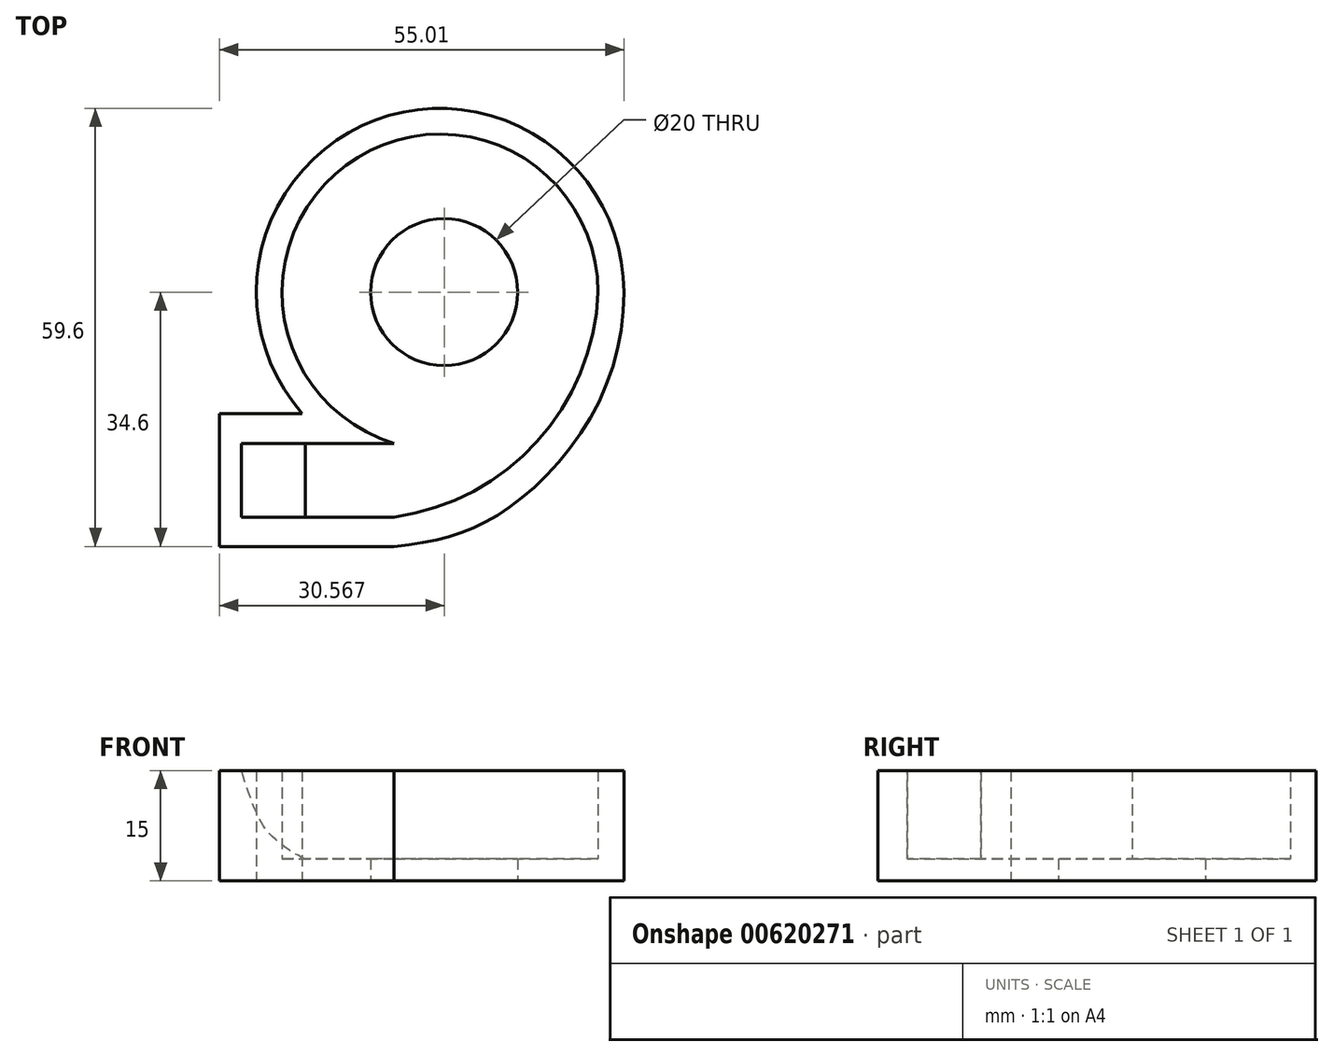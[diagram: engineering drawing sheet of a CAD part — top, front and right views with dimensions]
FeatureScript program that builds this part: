
annotation { "Feature Type Name" : "Feature", "Feature Type Description" : "" }
export const myFeature = defineFeature(function(context is Context, id is Id, definition is map)
    precondition{}
    {
        {
            var Q0;
            Q0=qCreatedBy(makeId("Top.planeOp"),FACE);
            var sketch = newSketch(context, id + "F0", { "sketchPlane" : qUnion([Q0])});
            skArc(sketch, "E0", {"start": v(25, 0) * mm, "mid": v(-8.82, 23.4) * mm, "end": v(-18.77, -16.5) * mm});
            skArc(sketch, "E1", {"start": v(21.5, 0) * mm, "mid": v(-12.8, 17.27) * mm, "end": v(-6.26, -20.57) * mm});
            skCircle(sketch, "E2", {"center": v(0.56, 0) * mm, "radius": 10 * mm});
            skPoint(sketch, "E3.first.point", {"position": v(21.5, 0) * mm});
            skPoint(sketch, "E3.second.point", {"position": v(-42.76, 1.57) * mm});
            skPoint(sketch, "E3.third.point", {"position": v(-6.26, -30.6) * mm});
            skArc(sketch, "E4", {"start": v(-6.27, -30.6) * mm, "mid": v(13.18, -20.36) * mm, "end": v(21.5, 0) * mm});
            skLineSegment(sketch, "E5", {"start": v(-6.27, -30.6) * mm, "end": v(-6.27, -30.6) * mm});
            skLineSegment(sketch, "E6", {"start": v(-6.26, -20.57) * mm, "end": v(-14.2, -20.57) * mm});
            skFitSpline(sketch, "E7", {"points": [v(25, 0) * mm, v(20.85, -16.4) * mm, v(11.12, -28.01) * mm, v(2.75, -32.8) * mm, v(-6.26, -34.6) * mm], "startDerivative": vector(0.09, -60.84) * mm, "endDerivative": vector(-48.17, -4.75) * mm});
            skLineSegment(sketch, "E8", {"start": v(-6.26, -30.6) * mm, "end": v(-23.34, -30.6) * mm});
            skLineSegment(sketch, "E9", {"start": v(-23.34, -20.57) * mm, "end": v(-14.2, -20.57) * mm});
            skLineSegment(sketch, "E10", {"start": v(-18.77, -16.5) * mm, "end": v(-27.01, -16.5) * mm});
            skLineSegment(sketch, "E11", {"start": v(-6.26, -34.6) * mm, "end": v(-27.01, -34.6) * mm});
            skLineSegment(sketch, "E12", {"start": v(-23.34, -20.57) * mm, "end": v(-27.01, -20.57) * mm});
            skLineSegment(sketch, "E13", {"start": v(-27.01, -30.6) * mm, "end": v(-23.34, -30.6) * mm});
            skLineSegment(sketch, "E14.trimOffspring", {"start": v(-27.01, -20.57) * mm, "end": v(-27.01, -16.5) * mm});
            skPoint(sketch, "E15.start.orphan", {"position": v(-18.77, -20.57) * mm});
            skLineSegment(sketch, "E16", {"start": v(-27.01, -30.6) * mm, "end": v(-27.01, -34.6) * mm});
            skLineSegment(sketch, "E17", {"start": v(-27.01, -21.39) * mm, "end": v(-27.01, -30.6) * mm});
            skLineSegment(sketch, "E18", {"start": v(-27.01, -21.39) * mm, "end": v(-27.01, -20.57) * mm});
            skSolve(sketch);
        }
        {
            var Q0;
            Q0=makeQuery(id+"F0.imprint","IMPRINT",FACE,{"disambiguationData":[TD([[makeQuery(id+"F0.imprint","IMPRINT",EDGE,{"derivedFrom":sQuery(id+"F0.wireOp",EDGE,"E0")}),1.0]])]});
            extrude(context, id + "F1", {"entities" : qUnion([Q0]), "depth" : 15 * mm, "offsetDistance" : 25 * mm});
        }
        {
            var Q0;
            {var subQ1=sQuery(id+"F0.wireOp",EDGE,"E1");Q0=makeQuery(id+"F0.imprint","IMPRINT",FACE,{"disambiguationData":[TD([[makeQuery(id+"F0.imprint","IMPRINT",EDGE,{"derivedFrom":subQ1}),1.0]])]});}
            extrude(context, id + "F2", {"entities" : qUnion([Q0]), "operationType" : NewBodyOperationType.ADD, "depth" : 3 * mm, "offsetDistance" : 25 * mm});
        }
        {
            var Q0;
            Q0=makeQuery(id+"F1.opExtrude","SWEPT_FACE",FACE,{"disambiguationData":[OSD([sQuery(id+"F0.wireOp",EDGE,"E8"),sQuery(id+"F0.wireOp",EDGE,"E13")])]});
            var sketch = newSketch(context, id + "F3", { "sketchPlane" : qUnion([Q0])});
            skFitSpline(sketch, "E19", {"points": [v(18.32, 3) * mm, v(22.8, 6) * mm, v(25.05, 9.42) * mm, v(27.01, 15) * mm], "startDerivative": vector(10.7, 3.57) * mm, "endDerivative": vector(4.94, 17.43) * mm});
            skSolve(sketch);
        }
        {
            var Q0;
            {var subQ0=sQuery(id+"F3.wireOp",EDGE,"E19");Q0=makeQuery(id+"F3.imprint","IMPRINT",FACE,{"disambiguationData":[TD([[makeQuery(id+"F3.imprint","IMPRINT",EDGE,{"derivedFrom":subQ0}),-1.0]])]});}
            extrude(context, id + "F4", {"entities" : qUnion([Q0]), "operationType" : NewBodyOperationType.ADD, "depth" : 11 * mm, "offsetDistance" : 25 * mm});
        }
        {
            var Q0;
            {var subQ0=sQuery(id+"F0.wireOp",EDGE,"E17");var subQ1=sQuery(id+"F0.wireOp",EDGE,"E16");Q0=makeQuery(id+"F4.boolean.opBoolean","MERGE",FACE,{"derivedFrom":[makeQuery(id+"F2.boolean.opBoolean","MERGE",FACE,{"derivedFrom":[makeQuery(id+"F1.opExtrude","SWEPT_FACE",FACE,{"disambiguationData":[OSD([sQuery(id+"F0.wireOp",EDGE,"E14.trimOffspring")])]}),makeQuery(id+"F1.opExtrude","SWEPT_FACE",FACE,{"disambiguationData":[OSD([subQ1])]}),makeQuery(id+"F2.opExtrude","SWEPT_FACE",FACE,{"disambiguationData":[OSD([subQ0,sQuery(id+"F0.wireOp",EDGE,"E18")])]})]}),makeQuery(id+"F4.opExtrude","SWEPT_FACE",FACE,{"disambiguationData":[OSD([sQuery(id+"F0.wireOp",EDGE,"E13"),subQ1,subQ0])]})]});}
            extrude(context, id + "F5", {"entities" : qUnion([Q0]), "operationType" : NewBodyOperationType.ADD, "depth" : 3 * mm, "offsetDistance" : 25 * mm});
        }
    });
